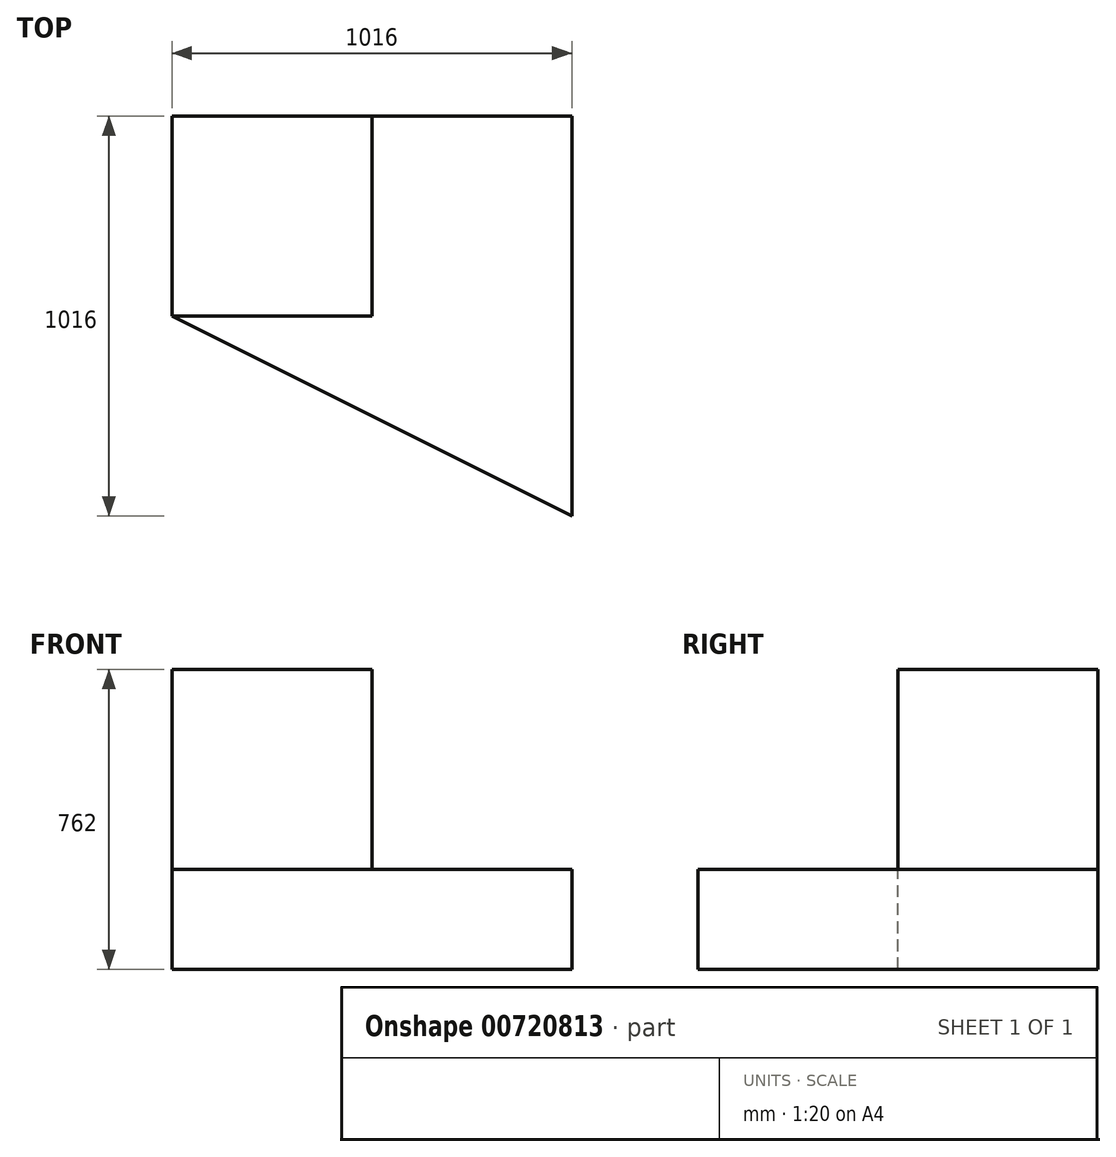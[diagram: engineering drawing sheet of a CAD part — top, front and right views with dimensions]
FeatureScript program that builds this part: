
annotation { "Feature Type Name" : "Feature", "Feature Type Description" : "" }
export const myFeature = defineFeature(function(context is Context, id is Id, definition is map)
    precondition{}
    {
        {
            var Q0;
            Q0=qCreatedBy(makeId("Top.planeOp"),FACE);
            var sketch = newSketch(context, id + "F0", { "sketchPlane" : qUnion([Q0])});
            skLineSegment(sketch, "E0.bottom", {"start": v(0, 0) * mm, "end": v(1016, 0) * mm});
            skLineSegment(sketch, "E0.top", {"start": v(0, -1016) * mm, "end": v(1016, -1016) * mm});
            skLineSegment(sketch, "E0.left", {"start": v(0, 0) * mm, "end": v(0, -1016) * mm});
            skLineSegment(sketch, "E0.right", {"start": v(1016, 0) * mm, "end": v(1016, -1016) * mm});
            skSolve(sketch);
        }
        {
            var Q0;
            Q0=makeQuery(id+"F0.imprint","IMPRINT",FACE,{"disambiguationData":[TD([[makeQuery(id+"F0.imprint","IMPRINT",EDGE,{"derivedFrom":sQuery(id+"F0.wireOp",EDGE,"E0.bottom")}),-1.0]])]});
            extrude(context, id + "F1", {"entities" : qUnion([Q0]), "depth" : 762 * mm, "offsetDistance" : 25.4 * mm});
        }
        {
            var Q0;
            Q0=makeQuery(id+"F1.opExtrude","CAP_FACE",FACE,{"disambiguationData":[OSD([sQuery(id+"F0.wireOp",EDGE,"E0.bottom"),sQuery(id+"F0.wireOp",EDGE,"E0.top"),sQuery(id+"F0.wireOp",EDGE,"E0.left"),sQuery(id+"F0.wireOp",EDGE,"E0.right")])],"isStart":false});
            var sketch = newSketch(context, id + "F2", { "sketchPlane" : qUnion([Q0])});
            skLineSegment(sketch, "E1.bottom", {"start": v(0, 0) * mm, "end": v(508, 0) * mm});
            skLineSegment(sketch, "E1.top", {"start": v(0, -508) * mm, "end": v(508, -508) * mm});
            skLineSegment(sketch, "E1.left", {"start": v(0, 0) * mm, "end": v(0, -508) * mm});
            skLineSegment(sketch, "E1.right", {"start": v(508, 0) * mm, "end": v(508, -508) * mm});
            skSolve(sketch);
        }
        {
            var Q0;
            {var subQ4=sQuery(id+"F2.wireOp",EDGE,"E1.top");Q0=makeQuery(id+"F2.imprint","IMPRINT",FACE,{"disambiguationData":[TD([[makeQuery(id+"F2.imprint","IMPRINT",EDGE,{"derivedFrom":subQ4}),-1.0]])]});}
            extrude(context, id + "F3", {"entities" : qUnion([Q0]), "operationType" : NewBodyOperationType.REMOVE, "oppositeDirection" : true, "depth" : 508 * mm, "offsetDistance" : 25.4 * mm});
        }
        {
            var Q0;
            Q0=makeQuery(id+"F3.boolean.opBoolean","COPY",FACE,{"derivedFrom":makeQuery(id+"F3.opExtrude","CAP_FACE",FACE,{"disambiguationData":[OSD([sQuery(id+"F0.wireOp",EDGE,"E0.bottom"),sQuery(id+"F0.wireOp",EDGE,"E0.top"),sQuery(id+"F0.wireOp",EDGE,"E0.left"),sQuery(id+"F0.wireOp",EDGE,"E0.right"),sQuery(id+"F2.wireOp",EDGE,"E1.top"),sQuery(id+"F2.wireOp",EDGE,"E1.right")])],"isStart":false})});
            var sketch = newSketch(context, id + "F4", { "sketchPlane" : qUnion([Q0])});
            skLineSegment(sketch, "E2", {"start": v(0, -508) * mm, "end": v(1016, -1016) * mm});
            skSolve(sketch);
        }
        {
            var Q0;
            Q0=makeQuery(id+"F4.imprint","IMPRINT",FACE,{"disambiguationData":[TD([[makeQuery(id+"F4.imprint","IMPRINT",EDGE,{"derivedFrom":sQuery(id+"F4.wireOp",EDGE,"E2")}),-1.0]])]});
            extrude(context, id + "F5", {"entities" : qUnion([Q0]), "operationType" : NewBodyOperationType.REMOVE, "oppositeDirection" : true, "depth" : 254 * mm, "offsetDistance" : 25.4 * mm});
        }
    });
